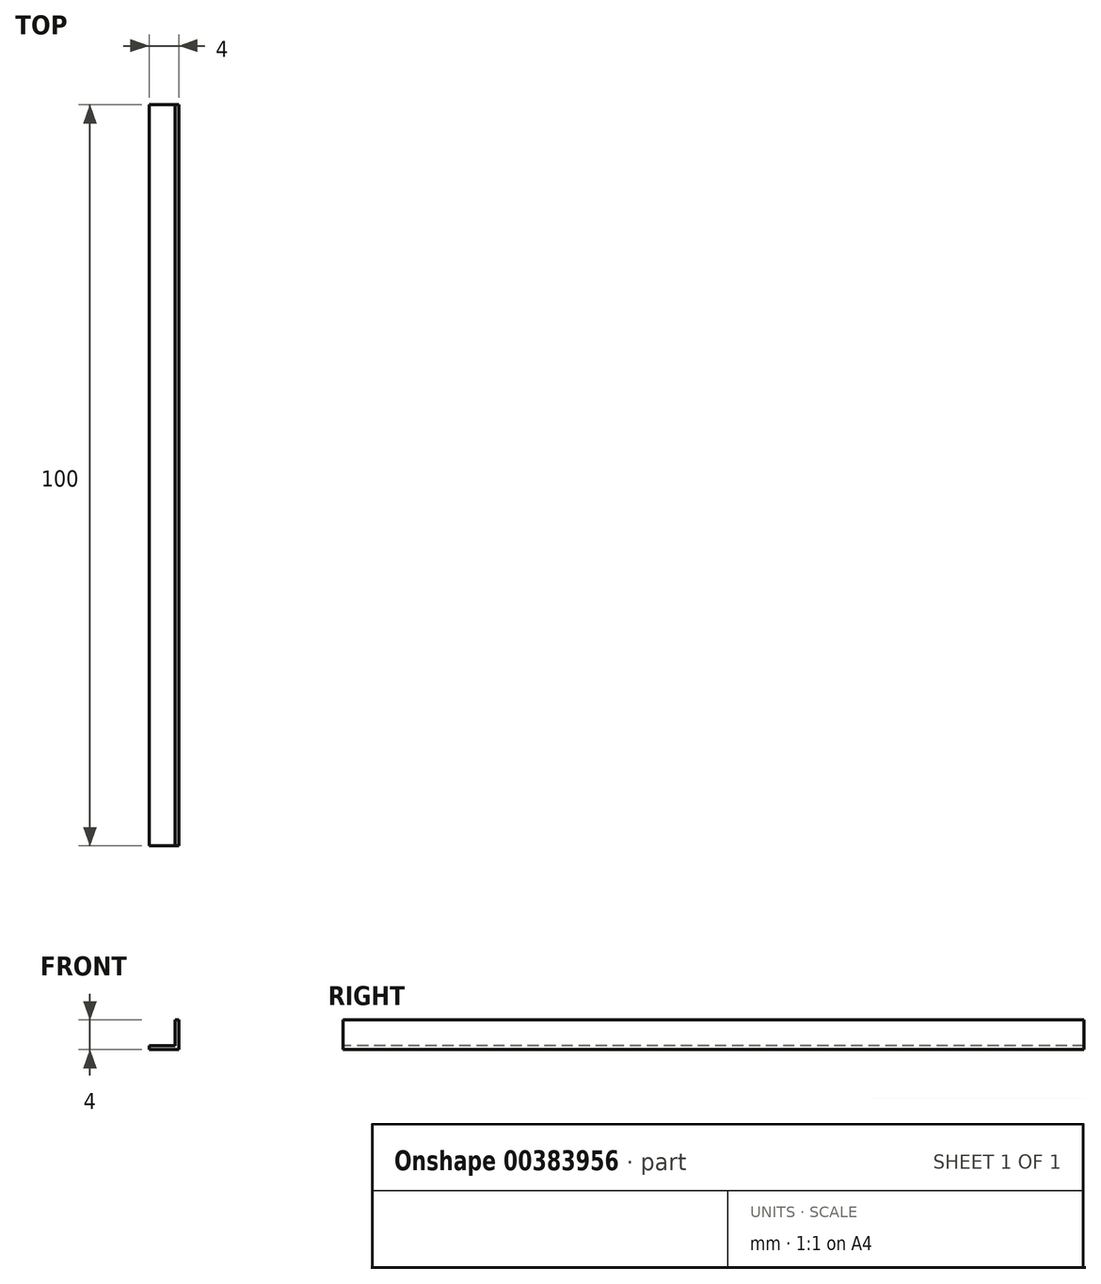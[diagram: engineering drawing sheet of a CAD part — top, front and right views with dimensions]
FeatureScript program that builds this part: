
annotation { "Feature Type Name" : "Feature", "Feature Type Description" : "" }
export const myFeature = defineFeature(function(context is Context, id is Id, definition is map)
    precondition{}
    {
        {
            var Q0;
            Q0=qCreatedBy(makeId("Top.planeOp"),FACE);
            var sketch = newSketch(context, id + "F0", { "sketchPlane" : qUnion([Q0])});
            skLineSegment(sketch, "E0", {"start": v(-33.05, 53.54) * mm, "end": v(-33.05, -46.46) * mm});
            skLineSegment(sketch, "E1", {"start": v(-33.05, 53.54) * mm, "end": v(-37.05, 53.54) * mm});
            skLineSegment(sketch, "E2", {"start": v(-37.05, 53.54) * mm, "end": v(-37.05, -46.46) * mm});
            skLineSegment(sketch, "E3", {"start": v(-37.05, -46.46) * mm, "end": v(-33.05, -46.46) * mm});
            skLineSegment(sketch, "E4", {"start": v(-33.55, 53.54) * mm, "end": v(-33.55, -46.46) * mm});
            skSolve(sketch);
        }
        {
            var Q0;
            {var subQ0=sQuery(id+"F0.wireOp",EDGE,"E2");Q0=makeQuery(id+"F0.imprint","IMPRINT",FACE,{"disambiguationData":[TD([[makeQuery(id+"F0.imprint","IMPRINT",EDGE,{"derivedFrom":subQ0}),1.0]])]});}
            extrude(context, id + "F1", {"entities" : qUnion([Q0]), "depth" : .5 * mm});
        }
        {
            var Q0;
            {var subQ0=sQuery(id+"F0.wireOp",EDGE,"E0");Q0=makeQuery(id+"F0.imprint","IMPRINT",FACE,{"disambiguationData":[TD([[makeQuery(id+"F0.imprint","IMPRINT",EDGE,{"derivedFrom":subQ0}),-1.0]])]});}
            extrude(context, id + "F2", {"entities" : qUnion([Q0]), "operationType" : NewBodyOperationType.ADD, "depth" : 4 * mm});
        }
    });
